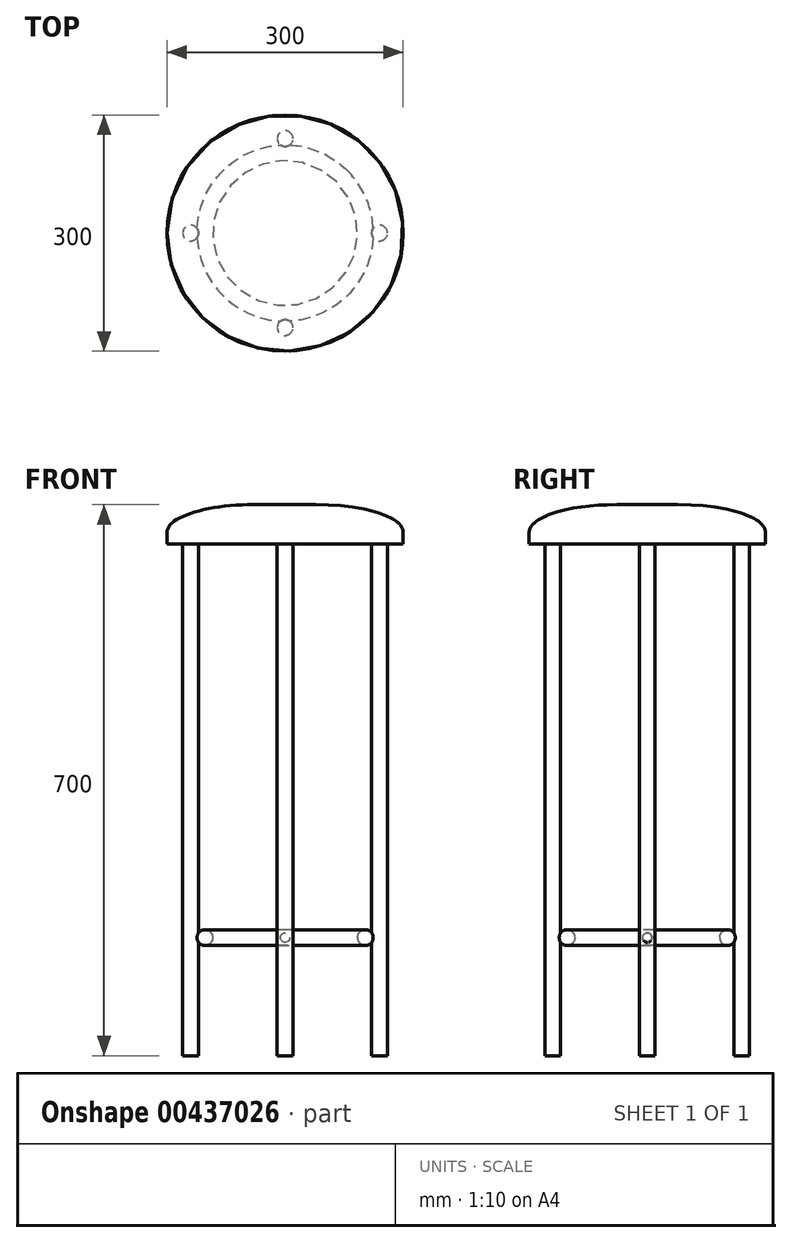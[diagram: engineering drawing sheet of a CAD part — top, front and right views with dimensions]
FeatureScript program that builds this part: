
annotation { "Feature Type Name" : "Feature", "Feature Type Description" : "" }
export const myFeature = defineFeature(function(context is Context, id is Id, definition is map)
    precondition{}
    {
        {
            var Q0;
            Q0=qCreatedBy(makeId("Front.planeOp"),FACE);
            var sketch = newSketch(context, id + "F0", { "sketchPlane" : qUnion([Q0])});
            skLineSegment(sketch, "E0", {"start": v(0, 0) * mm, "end": v(40, 0) * mm});
            skLineSegment(sketch, "E1", {"start": v(40, 0) * mm, "end": v(40, 15) * mm, "construction": true});
            skLineSegment(sketch, "E2", {"start": v(40, 15) * mm, "end": v(150, 15) * mm, "construction": true});
            skEllipticalArc(sketch, "E3", {});
            skLineSegment(sketch, "E4", {"start": v(150, 15) * mm, "end": v(150, 0) * mm});
            skLineSegment(sketch, "E5", {"start": v(150, 0) * mm, "end": v(0, 0) * mm});
            skLineSegment(sketch, "E6", {"start": v(0, 0) * mm, "end": v(0, 50) * mm});
            skPoint(sketch, "E6.endSnap0", {"position": v(40, 50) * mm});
            skLineSegment(sketch, "E7", {"start": v(0, 50) * mm, "end": v(40, 50) * mm});
            const initialGuessF0  = {"E3": [0.04, 0.015, 1, 0, 0.11, 0.035, 0, 1.5707963267948966]};
            skSetInitialGuess(sketch, initialGuessF0);
            skSolve(sketch);
        }
        {
            var Q0;
            Q0 = qSketchRegion(id + "F0", true);
            var Q1;
            Q1=sQuery(id+"F0.wireOp",EDGE,"E6");
            revolve(context, id + "F1", {"entities" : qUnion([Q0]), "axis" : qUnion([Q1]), "revolveType" : RevolveType.FULL});
        }
        {
            var Q0;
            Q0=makeQuery(id+"F1.opRevolve","SWEPT_FACE",FACE,{"disambiguationData":[OSD([sQuery(id+"F0.wireOp",EDGE,"E5")])]});
            var sketch = newSketch(context, id + "F2", { "sketchPlane" : qUnion([Q0])});
            skLineSegment(sketch, "E8", {"start": v(-150, 0) * mm, "end": v(150, 0) * mm, "construction": true});
            skLineSegment(sketch, "E9", {"start": v(0, 150) * mm, "end": v(0, -150) * mm, "construction": true});
            skCircle(sketch, "E10", {"center": v(0, 120) * mm, "radius": 10 * mm});
            skCircle(sketch, "E11.1.0", {"center": v(-120, 0) * mm, "radius": 10 * mm});
            skCircle(sketch, "E11.2.0", {"center": v(0, -120) * mm, "radius": 10 * mm});
            skPoint(sketch, "E11.center", {"position": v(0, 0) * mm});
            skCircle(sketch, "E12.1.3.0", {"center": v(120, 0) * mm, "radius": 10 * mm});
            skSolve(sketch);
        }
        {
            var Q0;
            Q0 = qSketchRegion(id + "F2", true);
            extrude(context, id + "F3", {"entities" : qUnion([Q0]), "operationType" : NewBodyOperationType.ADD, "depth" : 650 * mm});
        }
        {
            var Q0;
            Q0=makeQuery(id+"F1.opRevolve","SWEPT_FACE",FACE,{"disambiguationData":[OSD([sQuery(id+"F0.wireOp",EDGE,"E5")])]});
            cPlane(context, id + "F4", {"entities" : qUnion([Q0]), "cplaneType" : CPlaneType.OFFSET, "offset" : 500 * mm, "width" : 150 * mm, "height" : 150 * mm});
        }
        {
            var Q0;
            Q0=qCreatedBy(makeId("Front.planeOp"),FACE);
            var sketch = newSketch(context, id + "F5", { "sketchPlane" : qUnion([Q0])});
            skLineSegment(sketch, "E13", {"start": v(0, 0) * mm, "end": v(0, -500) * mm, "construction": true});
            skLineSegment(sketch, "E14", {"start": v(0, -500) * mm, "end": v(102, -500) * mm, "construction": true});
            skCircle(sketch, "E15", {"center": v(102, -500) * mm, "radius": 10 * mm});
            skSolve(sketch);
        }
        {
            var Q0;
            Q0 = qSketchRegion(id + "F5", true);
            var Q1;
            Q1=sQuery(id+"F5.wireOp",EDGE,"E13");
            revolve(context, id + "F6", {"operationType" : NewBodyOperationType.ADD, "entities" : qUnion([Q0]), "axis" : qUnion([Q1]), "revolveType" : RevolveType.FULL});
        }
    });
